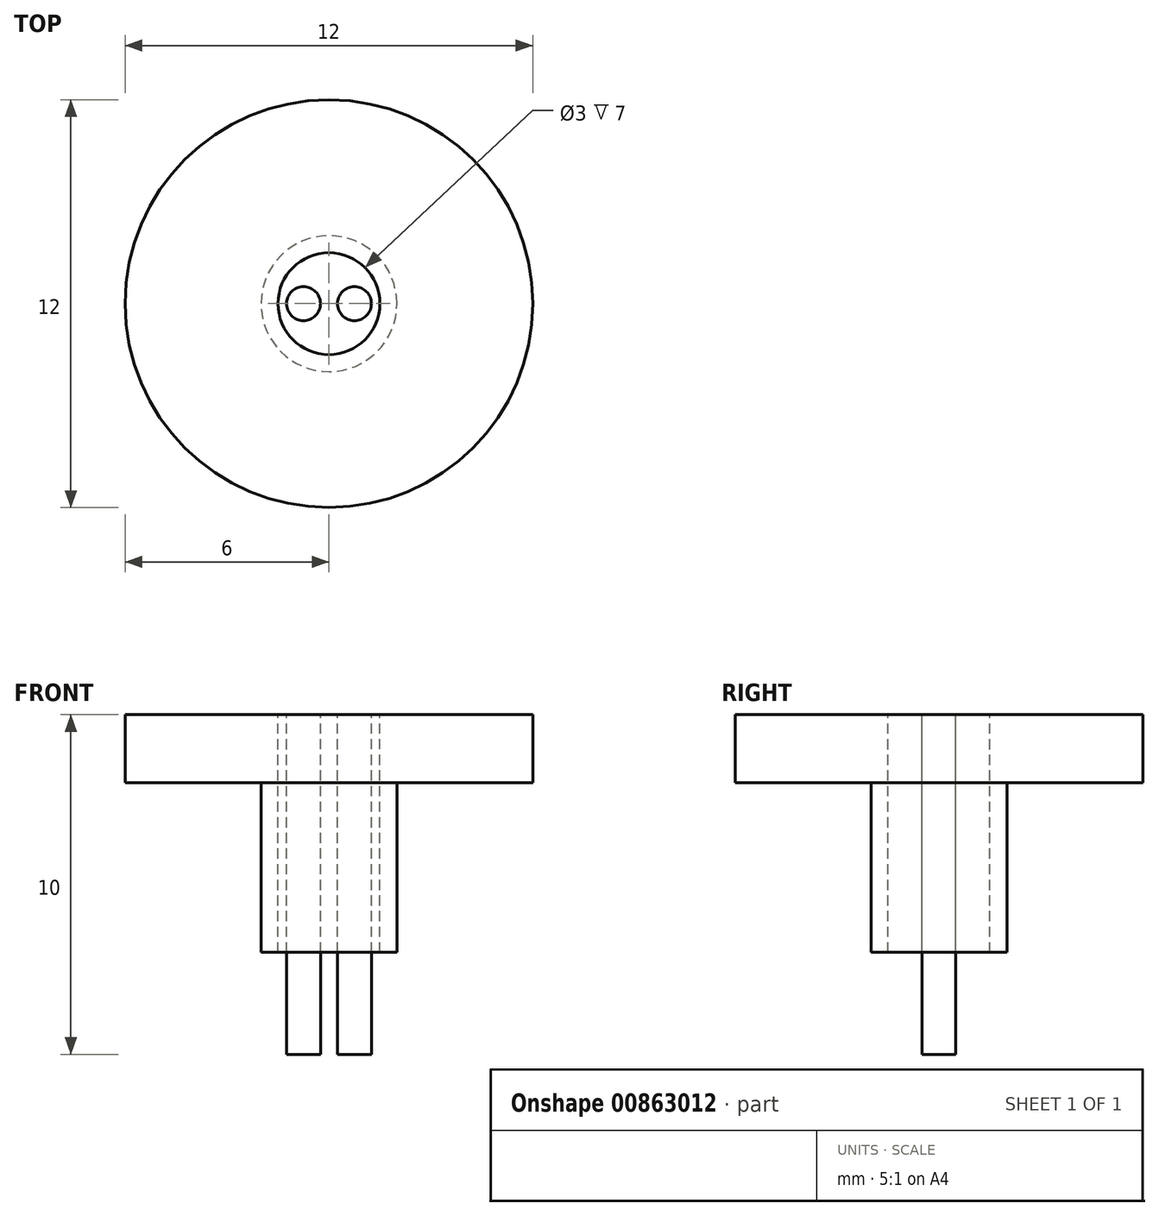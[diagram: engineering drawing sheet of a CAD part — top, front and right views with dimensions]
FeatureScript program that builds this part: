
annotation { "Feature Type Name" : "Feature", "Feature Type Description" : "" }
export const myFeature = defineFeature(function(context is Context, id is Id, definition is map)
    precondition{}
    {
        {
            var Q0;
            Q0=qCreatedBy(makeId("Top.planeOp"),FACE);
            var sketch = newSketch(context, id + "F0", { "sketchPlane" : qUnion([Q0])});
            skCircle(sketch, "E0", {"center": v(0, 0) * mm, "radius": 6 * mm});
            skSolve(sketch);
        }
        {
            var Q0;
            Q0 = qSketchRegion(id + "F0", true);
            extrude(context, id + "F1", {"entities" : qUnion([Q0]), "depth" : 2 * mm, "offsetDistance" : 25 * mm});
        }
        {
            var Q0;
            Q0=makeQuery(id+"F1.opExtrude","CAP_FACE",FACE,{"disambiguationData":[OSD([sQuery(id+"F0.wireOp",EDGE,"E0")])],"isStart":true});
            var sketch = newSketch(context, id + "F2", { "sketchPlane" : qUnion([Q0])});
            skCircle(sketch, "E1", {"center": v(0, 0) * mm, "radius": 2 * mm});
            skCircle(sketch, "E2", {"center": v(0, 0) * mm, "radius": 1.5 * mm});
            skSolve(sketch);
        }
        {
            var Q0;
            Q0 = qSketchRegion(id + "F2", true);
            extrude(context, id + "F3", {"entities" : qUnion([Q0]), "operationType" : NewBodyOperationType.ADD, "depth" : 5 * mm, "offsetDistance" : 25 * mm});
        }
        {
            var Q0;
            Q0=makeQuery(id+"F3.boolean.opBoolean","SPLIT",FACE,{"disambiguationData":[TD([makeQuery(id+"F3.opExtrude","SWEPT_FACE",FACE,{"disambiguationData":[OSD([sQuery(id+"F2.wireOp",EDGE,"E2")])]})])],"derivedFrom":makeQuery(id+"F1.opExtrude","CAP_FACE",FACE,{"disambiguationData":[OSD([sQuery(id+"F0.wireOp",EDGE,"E0")])],"isStart":true})});
            var sketch = newSketch(context, id + "F4", { "sketchPlane" : qUnion([Q0])});
            skCircle(sketch, "E3", {"center": v(0, 0) * mm, "radius": 1.5 * mm});
            skSolve(sketch);
        }
        {
            var Q0;
            Q0 = qSketchRegion(id + "F4", true);
            extrude(context, id + "F5", {"entities" : qUnion([Q0]), "operationType" : NewBodyOperationType.REMOVE, "oppositeDirection" : true, "depth" : 25 * mm, "offsetDistance" : 25 * mm});
        }
        {
            var Q0;
            Q0=makeQuery(id+"F1.opExtrude","CAP_FACE",FACE,{"disambiguationData":[OSD([sQuery(id+"F0.wireOp",EDGE,"E0")])],"isStart":false});
            var sketch = newSketch(context, id + "F6", { "sketchPlane" : qUnion([Q0])});
            skCircle(sketch, "E4", {"center": v(0, 0) * mm, "radius": 1.5 * mm});
            skCircle(sketch, "E5", {"center": v(-0.75, 0) * mm, "radius": 0.5 * mm});
            skCircle(sketch, "E6", {"center": v(0.75, 0) * mm, "radius": 0.5 * mm});
            skSolve(sketch);
        }
        {
            var Q0;
            Q0 = qSketchRegion(id + "F6", true);
            extrude(context, id + "F7", {"entities" : qUnion([Q0]), "oppositeDirection" : true, "depth" : 7 * mm, "offsetDistance" : 25 * mm});
        }
        {
            var Q0;
            Q0=makeQuery(id+"F1.opExtrude","CAP_FACE",FACE,{"disambiguationData":[OSD([sQuery(id+"F0.wireOp",EDGE,"E0")])],"isStart":false});
            var sketch = newSketch(context, id + "F8", { "sketchPlane" : qUnion([Q0])});
            skCircle(sketch, "E7", {"center": v(-0.75, 0) * mm, "radius": 0.5 * mm});
            skCircle(sketch, "E8", {"center": v(0.75, 0) * mm, "radius": 0.5 * mm});
            skSolve(sketch);
        }
        {
            var Q0;
            Q0 = qSketchRegion(id + "F8", true);
            extrude(context, id + "F9", {"entities" : qUnion([Q0]), "oppositeDirection" : true, "depth" : 10 * mm, "offsetDistance" : 25 * mm});
        }
    });
